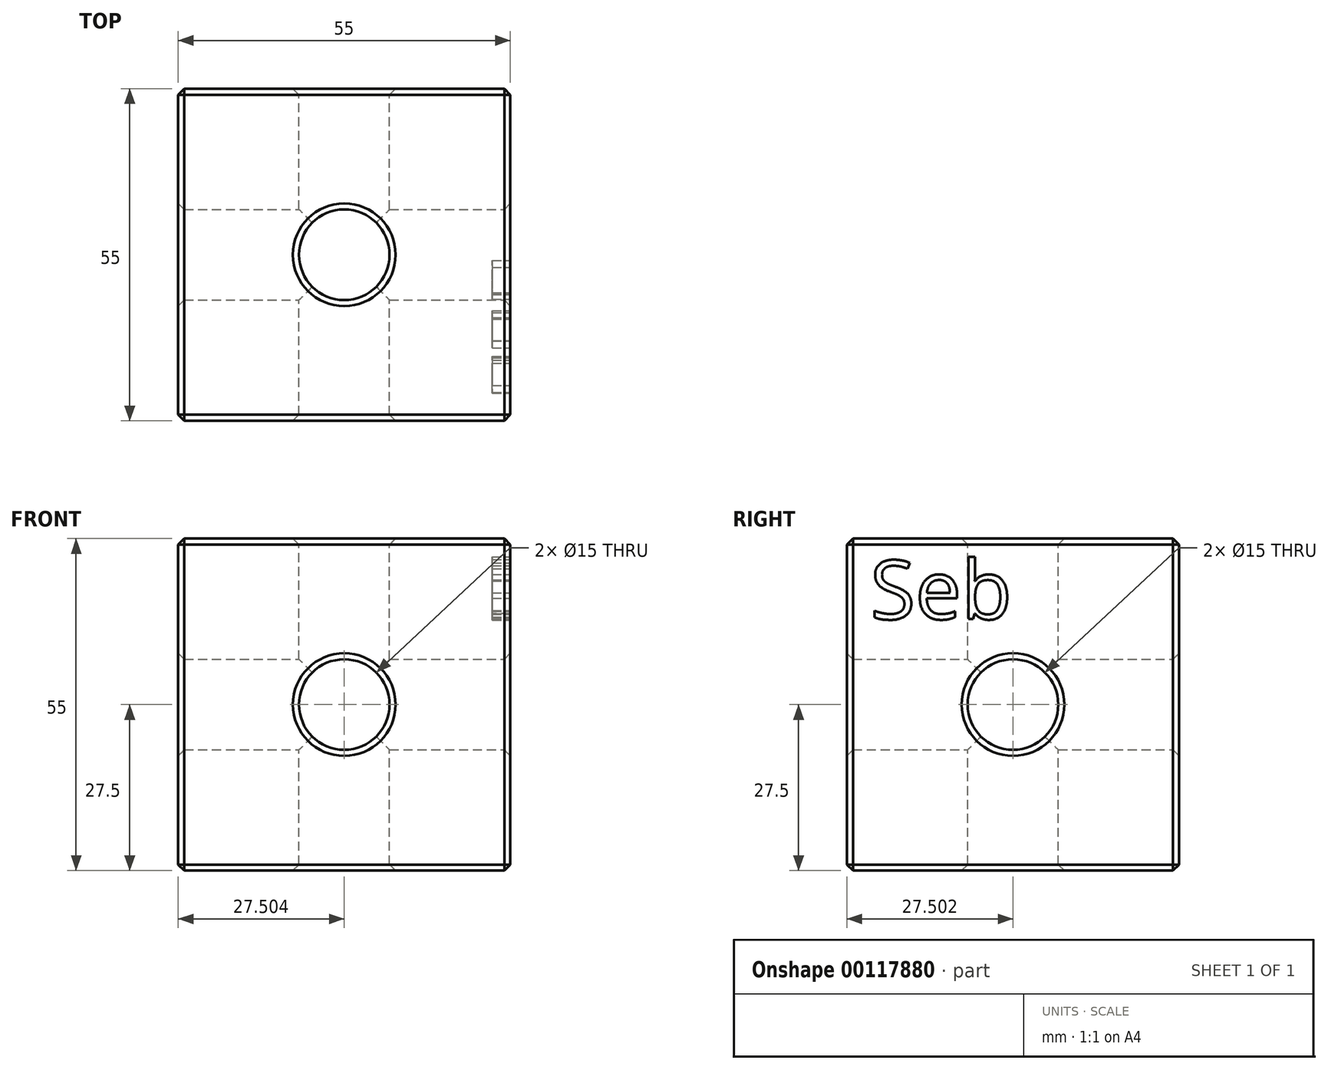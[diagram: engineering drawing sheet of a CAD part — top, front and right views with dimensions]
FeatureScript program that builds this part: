
annotation { "Feature Type Name" : "Feature", "Feature Type Description" : "" }
export const myFeature = defineFeature(function(context is Context, id is Id, definition is map)
    precondition{}
    {
        {
            var Q0;
            Q0=qCreatedBy(makeId("Top.planeOp"),FACE);
            var sketch = newSketch(context, id + "F0", { "sketchPlane" : qUnion([Q0])});
            skLineSegment(sketch, "E0.bottom", {"start": v(-30.8, -20.57) * mm, "end": v(24.2, -20.57) * mm});
            skLineSegment(sketch, "E0.top", {"start": v(-30.8, -75.57) * mm, "end": v(24.2, -75.57) * mm});
            skLineSegment(sketch, "E0.left", {"start": v(-30.8, -20.57) * mm, "end": v(-30.8, -75.57) * mm});
            skLineSegment(sketch, "E0.right", {"start": v(24.2, -20.57) * mm, "end": v(24.2, -75.57) * mm});
            skSolve(sketch);
        }
        {
            var Q0;
            Q0 = qSketchRegion(id + "F0", true);
            extrude(context, id + "F1", {"entities" : qUnion([Q0]), "depth" : 55 * mm});
        }
        {
            var Q0;
            Q0=makeQuery(id+"F1.opExtrude","CAP_FACE",FACE,{"disambiguationData":[OSD([sQuery(id+"F0.wireOp",EDGE,"E0.bottom"),sQuery(id+"F0.wireOp",EDGE,"E0.top"),sQuery(id+"F0.wireOp",EDGE,"E0.left"),sQuery(id+"F0.wireOp",EDGE,"E0.right")])],"isStart":false});
            var sketch = newSketch(context, id + "F2", { "sketchPlane" : qUnion([Q0])});
            skPoint(sketch, "E1", {"position": v(-3.3, -48.07) * mm});
            skPoint(sketch, "E2", {"position": v(24.2, -48.07) * mm});
            skPoint(sketch, "E3", {"position": v(-3.3, -75.57) * mm});
            skSolve(sketch);
        }
        {
            var Q0;
            Q0=sQuery(id+"F2.wireOp",VERTEX,"E1");
            var Q1;
            Q1=makeQuery(id+"F1.opExtrude","SWEPT_BODY",BODY,{"disambiguationData":[OSD([sQuery(id+"F0.wireOp",EDGE,"E0.bottom"),sQuery(id+"F0.wireOp",EDGE,"E0.top"),sQuery(id+"F0.wireOp",EDGE,"E0.left"),sQuery(id+"F0.wireOp",EDGE,"E0.right")])]});
            hole(context, id + "F3", {"style" : HoleStyle.SIMPLE, "endStyle" : HoleEndStyle.THROUGH, "holeDiameter" : 15 * mm, "locations" : qUnion([Q0]), "scope" : qUnion([Q1]), "isTappedThrough" : true});
        }
        {
            var Q0;
            Q0=makeQuery(id+"F1.opExtrude","SWEPT_FACE",FACE,{"disambiguationData":[OSD([sQuery(id+"F0.wireOp",EDGE,"E0.right")])]});
            var sketch = newSketch(context, id + "F4", { "sketchPlane" : qUnion([Q0])});
            skPoint(sketch, "E4", {"position": v(-48.07, 27.5) * mm});
            skPoint(sketch, "E4.positionSnap0", {"position": v(-48.07, 55) * mm});
            skPoint(sketch, "E4.positionSnap1", {"position": v(-20.57, 27.5) * mm});
            skText(sketch, "E5", { "text": "Seb", "fontName": "OpenSans-Regular.ttf"});
            const initialGuessF4  = {"E5": [-0.07172, 0.04165, 1, 0, 0.0098]};
            skSetInitialGuess(sketch, initialGuessF4);
            skSolve(sketch);
        }
        {
            var Q0;
            Q0=sQuery(id+"F4.wireOp",VERTEX,"E4");
            var Q1;
            Q1=makeQuery(id+"F1.opExtrude","SWEPT_BODY",BODY,{"disambiguationData":[OSD([sQuery(id+"F0.wireOp",EDGE,"E0.bottom"),sQuery(id+"F0.wireOp",EDGE,"E0.top"),sQuery(id+"F0.wireOp",EDGE,"E0.left"),sQuery(id+"F0.wireOp",EDGE,"E0.right")])]});
            hole(context, id + "F5", {"style" : HoleStyle.SIMPLE, "endStyle" : HoleEndStyle.THROUGH, "holeDiameter" : 15 * mm, "locations" : qUnion([Q0]), "scope" : qUnion([Q1]), "isTappedThrough" : true});
        }
        {
            var Q0;
            Q0=makeQuery(id+"F1.opExtrude","SWEPT_FACE",FACE,{"disambiguationData":[OSD([sQuery(id+"F0.wireOp",EDGE,"E0.bottom")])]});
            var sketch = newSketch(context, id + "F6", { "sketchPlane" : qUnion([Q0])});
            skPoint(sketch, "E6", {"position": v(3.3, 27.5) * mm});
            skPoint(sketch, "E6.positionSnap0", {"position": v(3.3, 55) * mm});
            skPoint(sketch, "E6.positionSnap1", {"position": v(30.8, 27.5) * mm});
            skSolve(sketch);
        }
        {
            var Q0;
            Q0=sQuery(id+"F6.wireOp",VERTEX,"E6");
            var Q1;
            Q1=makeQuery(id+"F1.opExtrude","SWEPT_BODY",BODY,{"disambiguationData":[OSD([sQuery(id+"F0.wireOp",EDGE,"E0.bottom"),sQuery(id+"F0.wireOp",EDGE,"E0.top"),sQuery(id+"F0.wireOp",EDGE,"E0.left"),sQuery(id+"F0.wireOp",EDGE,"E0.right")])]});
            hole(context, id + "F7", {"style" : HoleStyle.SIMPLE, "endStyle" : HoleEndStyle.THROUGH, "holeDiameter" : 15 * mm, "locations" : qUnion([Q0]), "scope" : qUnion([Q1]), "isTappedThrough" : true});
        }
        {
            var Q0;
            Q0=makeQuery(id+"F1.opExtrude","CAP_FACE",FACE,{"disambiguationData":[OSD([sQuery(id+"F0.wireOp",EDGE,"E0.bottom"),sQuery(id+"F0.wireOp",EDGE,"E0.top"),sQuery(id+"F0.wireOp",EDGE,"E0.left"),sQuery(id+"F0.wireOp",EDGE,"E0.right")])],"isStart":false});
            var Q1;
            Q1=makeQuery(id+"F1.opExtrude","SWEPT_FACE",FACE,{"disambiguationData":[OSD([sQuery(id+"F0.wireOp",EDGE,"E0.top")])]});
            var Q2;
            Q2=makeQuery(id+"F1.opExtrude","SWEPT_FACE",FACE,{"disambiguationData":[OSD([sQuery(id+"F0.wireOp",EDGE,"E0.right")])]});
            var Q3;
            Q3=makeQuery(id+"F1.opExtrude","SWEPT_FACE",FACE,{"disambiguationData":[OSD([sQuery(id+"F0.wireOp",EDGE,"E0.bottom")])]});
            var Q4;
            Q4=makeQuery(id+"F1.opExtrude","SWEPT_FACE",FACE,{"disambiguationData":[OSD([sQuery(id+"F0.wireOp",EDGE,"E0.left")])]});
            var Q5;
            Q5=makeQuery(id+"F1.opExtrude","CAP_FACE",FACE,{"disambiguationData":[OSD([sQuery(id+"F0.wireOp",EDGE,"E0.bottom"),sQuery(id+"F0.wireOp",EDGE,"E0.top"),sQuery(id+"F0.wireOp",EDGE,"E0.left"),sQuery(id+"F0.wireOp",EDGE,"E0.right")])],"isStart":true});
            chamfer(context, id + "F8", {"entities" : qUnion([Q0, Q1, Q2, Q3, Q4, Q5]), "width" : 1 * mm, "tangentPropagation" : true});
        }
        {
            var Q0;
            Q0 = qSketchRegion(id + "F4", true);
            extrude(context, id + "F9", {"entities" : qUnion([Q0]), "operationType" : NewBodyOperationType.REMOVE, "oppositeDirection" : true, "depth" : 3 * mm});
        }
    });
